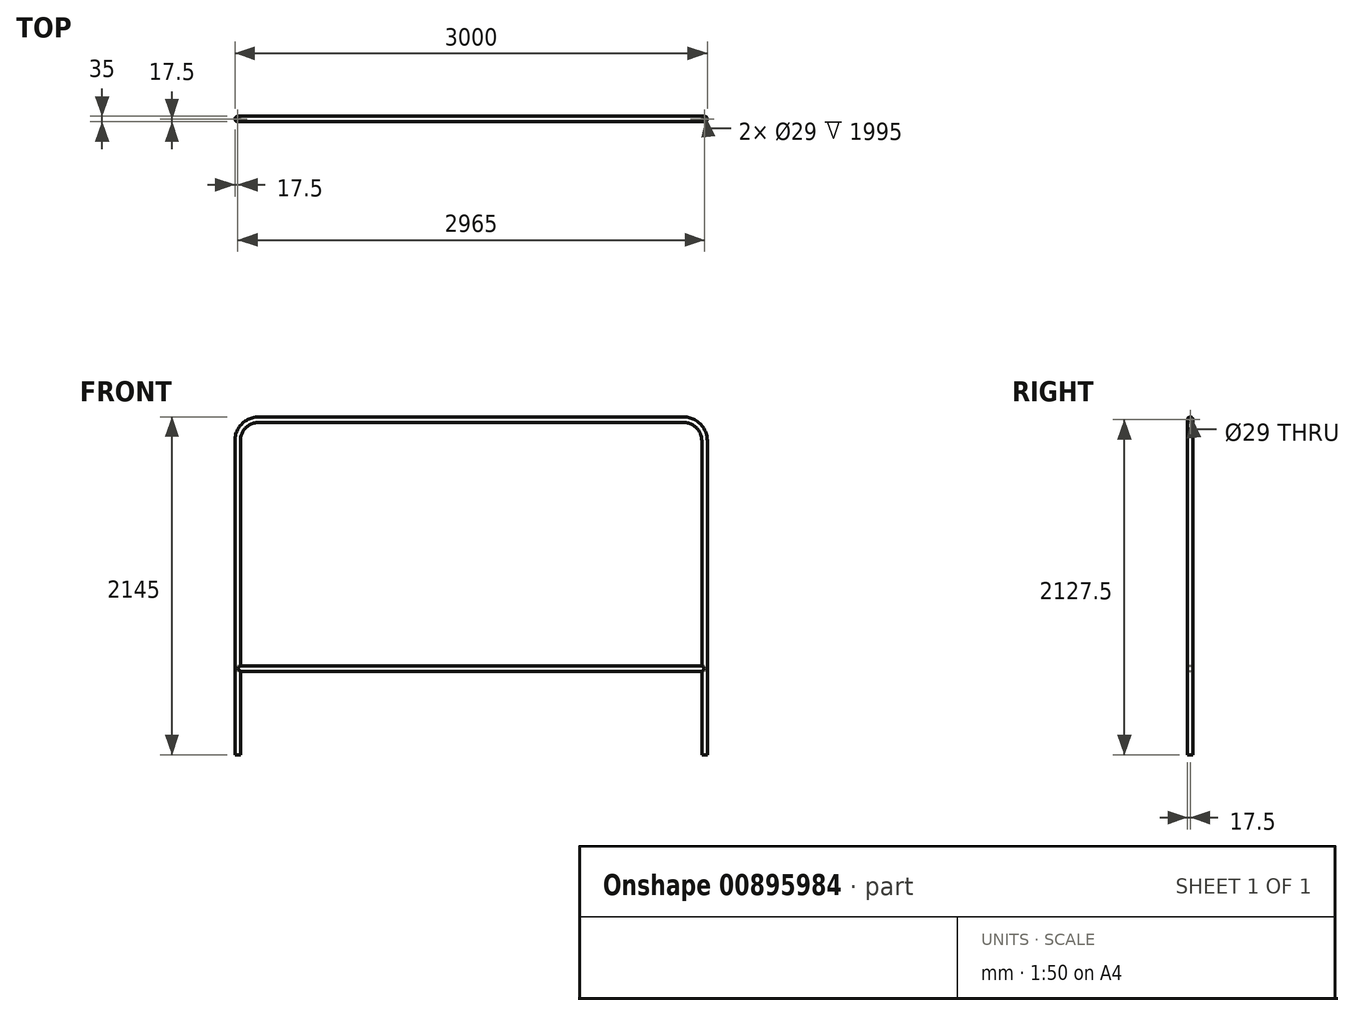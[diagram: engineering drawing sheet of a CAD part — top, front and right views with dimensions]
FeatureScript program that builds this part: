
annotation { "Feature Type Name" : "Feature", "Feature Type Description" : "" }
export const myFeature = defineFeature(function(context is Context, id is Id, definition is map)
    precondition{}
    {
        {
            var Q0;
            Q0=qCreatedBy(makeId("Front.planeOp"),FACE);
            var sketch = newSketch(context, id + "F0", { "sketchPlane" : qUnion([Q0])});
            skLineSegment(sketch, "E0", {"start": v(-1482.5, 0) * mm, "end": v(-1482.5, 1995) * mm});
            skLineSegment(sketch, "E1", {"start": v(-1350, 2127.5) * mm, "end": v(0, 2127.5) * mm});
            skPoint(sketch, "E2.visualSharp", {"position": v(-1482.5, 2127.5) * mm});
            skArc(sketch, "E2.filletArc", {"start": v(-1350, 2127.5) * mm, "mid": v(-1443.7, 2088.7) * mm, "end": v(-1482.5, 1995) * mm});
            skLineSegment(sketch, "E3.MirrorCS", {"start": v(1350, 2127.5) * mm, "end": v(0, 2127.5) * mm});
            skPoint(sketch, "E4.MirrorP", {"position": v(1482.5, 2127.5) * mm});
            skArc(sketch, "E5.MirrorCS", {"start": v(1350, 2127.5) * mm, "mid": v(1443.7, 2088.7) * mm, "end": v(1482.5, 1995) * mm});
            skLineSegment(sketch, "E6.MirrorCS", {"start": v(1482.5, 0) * mm, "end": v(1482.5, 1995) * mm});
            skSolve(sketch);
        }
        {
            var Q0;
            Q0=qCreatedBy(makeId("Top.planeOp"),FACE);
            var sketch = newSketch(context, id + "F1", { "sketchPlane" : qUnion([Q0])});
            skCircle(sketch, "E7", {"center": v(-1482.5, 0) * mm, "radius": 17.5 * mm});
            skCircle(sketch, "E8", {"center": v(-1482.5, 0) * mm, "radius": 14.5 * mm});
            skSolve(sketch);
        }
        {
            var Q0;
            Q0=makeQuery(id+"F1.imprint","IMPRINT",FACE,{"disambiguationData":[TD([[makeQuery(id+"F1.imprint","IMPRINT",EDGE,{"derivedFrom":sQuery(id+"F1.wireOp",EDGE,"E7")}),1.0]])]});
            var Q1;
            Q1=sQuery(id+"F0.wireOp",EDGE,"E0");
            var Q2;
            Q2=sQuery(id+"F0.wireOp",EDGE,"E2.filletArc");
            var Q3;
            Q3=sQuery(id+"F0.wireOp",EDGE,"E1");
            var Q4;
            Q4=sQuery(id+"F0.wireOp",EDGE,"E3.MirrorCS");
            var Q5;
            Q5=sQuery(id+"F0.wireOp",EDGE,"E5.MirrorCS");
            var Q6;
            Q6=sQuery(id+"F0.wireOp",EDGE,"E6.MirrorCS");
            sweep(context, id + "F2", {"profiles" : qUnion([Q0]), "path" : qUnion([Q1, Q2, Q3, Q4, Q5, Q6])});
        }
        {
            var Q0;
            Q0=qCreatedBy(makeId("Right.planeOp"),FACE);
            var sketch = newSketch(context, id + "F3", { "sketchPlane" : qUnion([Q0])});
            skCircle(sketch, "E9", {"center": v(0, 547.5) * mm, "radius": 17.5 * mm});
            skSolve(sketch);
        }
        {
            var Q0;
            Q0 = qSketchRegion(id + "F3", true);
            extrude(context, id + "F4", {"entities" : qUnion([Q0]), "operationType" : NewBodyOperationType.ADD, "endBound" : BoundingType.SYMMETRIC, "depth" : 2965 * mm, "offsetDistance" : 25 * mm});
        }
    });
